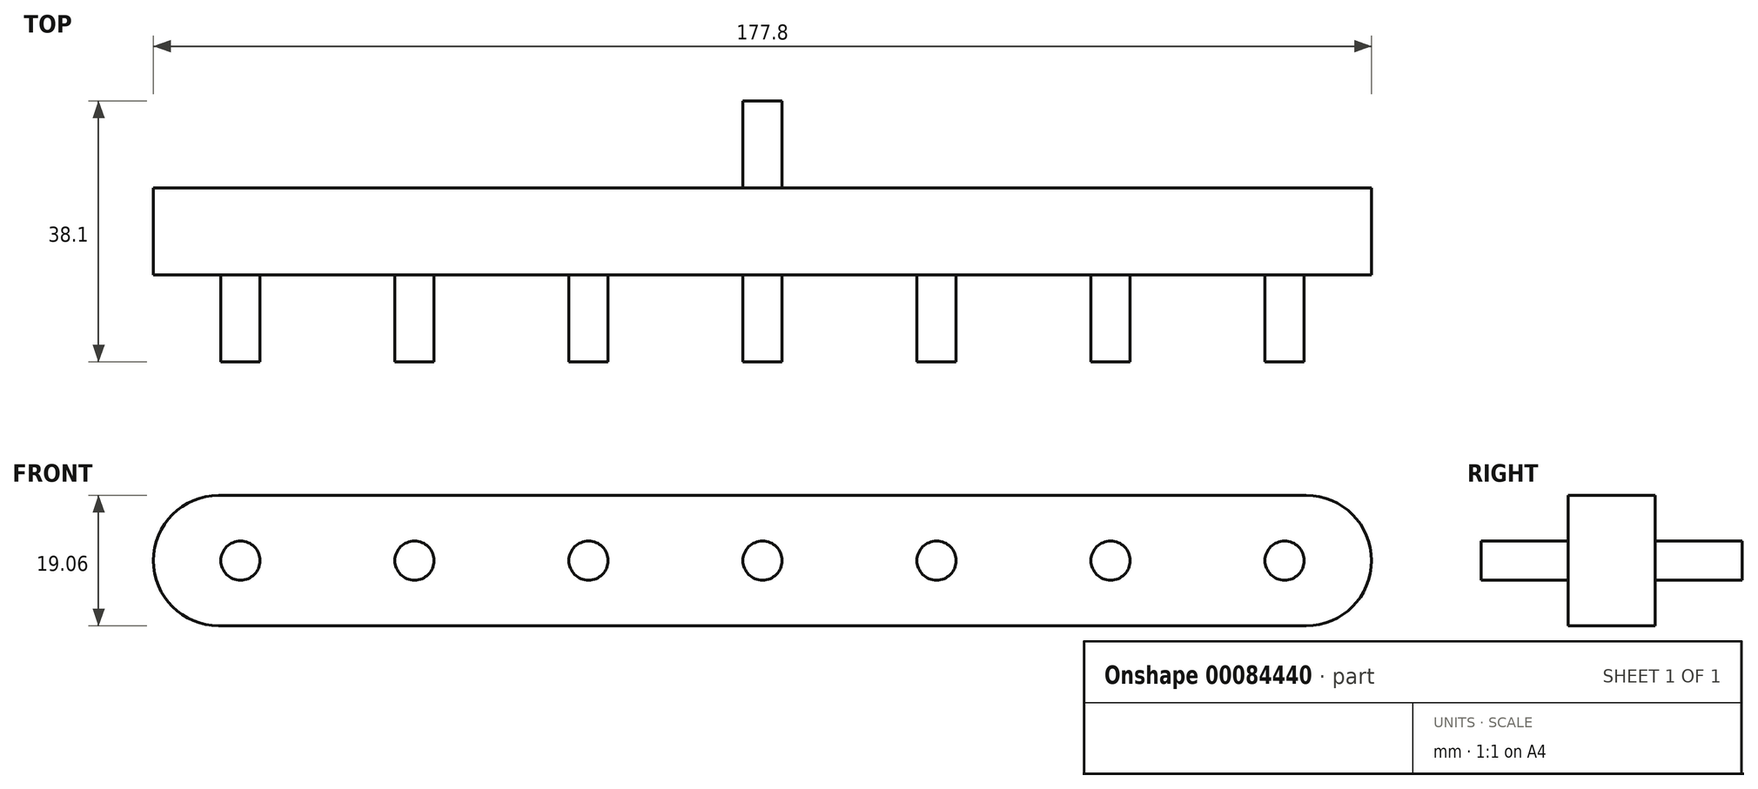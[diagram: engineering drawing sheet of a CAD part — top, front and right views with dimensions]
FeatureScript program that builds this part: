
annotation { "Feature Type Name" : "Feature", "Feature Type Description" : "" }
export const myFeature = defineFeature(function(context is Context, id is Id, definition is map)
    precondition{}
    {
        {
            var Q0;
            Q0=qCreatedBy(makeId("Front.planeOp"),FACE);
            var sketch = newSketch(context, id + "F0", { "sketchPlane" : qUnion([Q0])});
            skLineSegment(sketch, "E0.bottom", {"start": v(88.9, -9.52) * mm, "end": v(-88.9, -9.52) * mm});
            skLineSegment(sketch, "E0.top", {"start": v(88.9, 9.53) * mm, "end": v(-88.9, 9.53) * mm});
            skLineSegment(sketch, "E0.left", {"start": v(88.9, -9.52) * mm, "end": v(88.9, 9.53) * mm});
            skLineSegment(sketch, "E0.right", {"start": v(-88.9, -9.52) * mm, "end": v(-88.9, 9.53) * mm});
            skPoint(sketch, "E1.middle", {"position": v(0, 0) * mm});
            skLineSegment(sketch, "E2", {"start": v(0, 0) * mm, "end": v(0, 0) * mm});
            skCircle(sketch, "E3", {"center": v(0, 0) * mm, "radius": 2.86 * mm});
            skCircle(sketch, "E4.1.0.0", {"center": v(25.4, 0) * mm, "radius": 2.86 * mm});
            skCircle(sketch, "E4.2.0.0", {"center": v(50.8, 0) * mm, "radius": 2.86 * mm});
            skLineSegment(sketch, "E4.direction1", {"start": v(0, 0) * mm, "end": v(25.4, 0) * mm, "construction": true});
            skCircle(sketch, "E5.0.3.0", {"center": v(76.2, 0) * mm, "radius": 2.86 * mm});
            skCircle(sketch, "E6.1.0.0", {"center": v(-25.4, 0) * mm, "radius": 2.86 * mm});
            skCircle(sketch, "E6.2.0.0", {"center": v(-50.8, 0) * mm, "radius": 2.86 * mm});
            skLineSegment(sketch, "E6.direction1", {"start": v(0, 0) * mm, "end": v(-25.4, 0) * mm, "construction": true});
            skCircle(sketch, "E7.0.3.0", {"center": v(-76.2, 0) * mm, "radius": 2.86 * mm});
            skLineSegment(sketch, "E8", {"start": v(0, 0) * mm, "end": v(0, 9.53) * mm});
            skSolve(sketch);
        }
        {
            var Q0;
            Q0=makeQuery(id+"F0.imprint","IMPRINT",FACE,{"disambiguationData":[TD([[makeQuery(id+"F0.imprint","IMPRINT",EDGE,{"derivedFrom":sQuery(id+"F0.wireOp",EDGE,"SHm8Pa34-JDRi-xLCb-vY8M-4y8iot5nddfY")}),1.0]])]});
            var Q1;
            Q1=makeQuery(id+"F0.imprint","IMPRINT",FACE,{"disambiguationData":[TD([[makeQuery(id+"F0.imprint","IMPRINT",EDGE,{"derivedFrom":sQuery(id+"F0.wireOp",EDGE,"E0.bottom")}),-1.0]])]});
            var Q2;
            Q2=makeQuery(id+"F0.imprint","IMPRINT",FACE,{"disambiguationData":[TD([[makeQuery(id+"F0.imprint","IMPRINT",EDGE,{"derivedFrom":sQuery(id+"F0.wireOp",EDGE,"yVfw5L5J-6KiR-xsoj-KyT5-XFOPuA5cFtkD")}),1.0]])]});
            var Q3;
            Q3=makeQuery(id+"F0.imprint","IMPRINT",FACE,{"disambiguationData":[TD([[makeQuery(id+"F0.imprint","IMPRINT",EDGE,{"derivedFrom":sQuery(id+"F0.wireOp",EDGE,"otzoMOgJ-2Fw9-6XRC-HHPs-JyfjwHity7ub")}),1.0]])]});
            extrude(context, id + "F1", {"entities" : qUnion([Q0, Q1, Q2, Q3]), "depth" : 12.7 * mm});
        }
        {
            var Q0;
            Q0=makeQuery(id+"F0.imprint","IMPRINT",FACE,{"disambiguationData":[TD([[makeQuery(id+"F0.imprint","IMPRINT",EDGE,{"derivedFrom":sQuery(id+"F0.wireOp",EDGE,"E3")}),1.0]])]});
            var Q1;
            Q1=makeQuery(id+"F0.imprint","IMPRINT",FACE,{"disambiguationData":[TD([[makeQuery(id+"F0.imprint","IMPRINT",EDGE,{"derivedFrom":sQuery(id+"F0.wireOp",EDGE,"W0BhPmkZ-Cohu-r3UB-MNsT-8zEHgvukqrbW")}),1.0]])]});
            var Q2;
            Q2=makeQuery(id+"F0.imprint","IMPRINT",FACE,{"disambiguationData":[TD([[makeQuery(id+"F0.imprint","IMPRINT",EDGE,{"derivedFrom":sQuery(id+"F0.wireOp",EDGE,"otzoMOgJ-2Fw9-6XRC-HHPs-JyfjwHity7ub")}),1.0]])]});
            var Q3;
            Q3=makeQuery(id+"F0.imprint","IMPRINT",FACE,{"disambiguationData":[TD([[makeQuery(id+"F0.imprint","IMPRINT",EDGE,{"derivedFrom":sQuery(id+"F0.wireOp",EDGE,"3Px4a1Am-neuG-O9X5-1E42-bK21xOlIPYbs")}),1.0]])]});
            var Q4;
            Q4=makeQuery(id+"F0.imprint","IMPRINT",FACE,{"disambiguationData":[TD([[makeQuery(id+"F0.imprint","IMPRINT",EDGE,{"derivedFrom":sQuery(id+"F0.wireOp",EDGE,"TvybUxnP-oc0P-UiPS-1L8a-IxXoS0crJDyP")}),1.0]])]});
            var Q5;
            Q5=makeQuery(id+"F0.imprint","IMPRINT",FACE,{"disambiguationData":[TD([[makeQuery(id+"F0.imprint","IMPRINT",EDGE,{"derivedFrom":sQuery(id+"F0.wireOp",EDGE,"yVfw5L5J-6KiR-xsoj-KyT5-XFOPuA5cFtkD")}),1.0]])]});
            var Q6;
            Q6=makeQuery(id+"F0.imprint","IMPRINT",FACE,{"disambiguationData":[TD([[makeQuery(id+"F0.imprint","IMPRINT",EDGE,{"derivedFrom":sQuery(id+"F0.wireOp",EDGE,"E7.0.4.0")}),1.0]])]});
            var Q7;
            Q7=makeQuery(id+"F0.imprint","IMPRINT",FACE,{"disambiguationData":[TD([[makeQuery(id+"F0.imprint","IMPRINT",EDGE,{"derivedFrom":sQuery(id+"F0.wireOp",EDGE,"E7.0.3.0")}),1.0]])]});
            var Q8;
            Q8=makeQuery(id+"F0.imprint","IMPRINT",FACE,{"disambiguationData":[TD([[makeQuery(id+"F0.imprint","IMPRINT",EDGE,{"derivedFrom":sQuery(id+"F0.wireOp",EDGE,"E6.2.0.0")}),1.0]])]});
            var Q9;
            Q9=makeQuery(id+"F0.imprint","IMPRINT",FACE,{"disambiguationData":[TD([[makeQuery(id+"F0.imprint","IMPRINT",EDGE,{"derivedFrom":sQuery(id+"F0.wireOp",EDGE,"E6.1.0.0")}),1.0]])]});
            var Q10;
            Q10=makeQuery(id+"F0.imprint","IMPRINT",FACE,{"disambiguationData":[TD([[makeQuery(id+"F0.imprint","IMPRINT",EDGE,{"derivedFrom":sQuery(id+"F0.wireOp",EDGE,"E4.1.0.0")}),1.0]])]});
            var Q11;
            Q11=makeQuery(id+"F0.imprint","IMPRINT",FACE,{"disambiguationData":[TD([[makeQuery(id+"F0.imprint","IMPRINT",EDGE,{"derivedFrom":sQuery(id+"F0.wireOp",EDGE,"E4.2.0.0")}),1.0]])]});
            var Q12;
            Q12=makeQuery(id+"F0.imprint","IMPRINT",FACE,{"disambiguationData":[TD([[makeQuery(id+"F0.imprint","IMPRINT",EDGE,{"derivedFrom":sQuery(id+"F0.wireOp",EDGE,"E5.0.3.0")}),1.0]])]});
            var Q13;
            Q13=makeQuery(id+"F0.imprint","IMPRINT",FACE,{"disambiguationData":[TD([[makeQuery(id+"F0.imprint","IMPRINT",EDGE,{"derivedFrom":sQuery(id+"F0.wireOp",EDGE,"E5.0.4.0")}),1.0]])]});
            extrude(context, id + "F2", {"entities" : qUnion([Q0, Q1, Q2, Q3, Q4, Q5, Q6, Q7, Q8, Q9, Q10, Q11, Q12, Q13]), "operationType" : NewBodyOperationType.ADD, "depth" : 25.4 * mm});
        }
        {
            var Q0;
            {var subQ0=sQuery(id+"F0.wireOp",EDGE,"3Px4a1Am-neuG-O9X5-1E42-bK21xOlIPYbs");var subQ1=sQuery(id+"F0.wireOp",EDGE,"E3");var subQ2=sQuery(id+"F0.wireOp",EDGE,"TvybUxnP-oc0P-UiPS-1L8a-IxXoS0crJDyP");Q0=makeQuery(id+"F2.boolean.opBoolean","MERGE",FACE,{"derivedFrom":[makeQuery(id+"F1.opExtrude","CAP_FACE",FACE,{"disambiguationData":[OSD([sQuery(id+"F0.wireOp",EDGE,"E0.bottom"),sQuery(id+"F0.wireOp",EDGE,"E0.top"),sQuery(id+"F0.wireOp",EDGE,"E0.left"),sQuery(id+"F0.wireOp",EDGE,"E0.right"),subQ2,subQ1,subQ0])],"isStart":true}),makeQuery(id+"F2.opExtrude","CAP_FACE",FACE,{"disambiguationData":[OSD([subQ2])],"isStart":true}),makeQuery(id+"F2.opExtrude","CAP_FACE",FACE,{"disambiguationData":[OSD([subQ1])],"isStart":true}),makeQuery(id+"F2.opExtrude","CAP_FACE",FACE,{"disambiguationData":[OSD([subQ0])],"isStart":true})]});}
            var sketch = newSketch(context, id + "F3", { "sketchPlane" : qUnion([Q0])});
            skLineSegment(sketch, "E9", {"start": v(0, 0) * mm, "end": v(0, 0) * mm});
            skCircle(sketch, "E10", {"center": v(0, 0) * mm, "radius": 2.86 * mm});
            skSolve(sketch);
        }
        {
            var Q0;
            Q0=makeQuery(id+"F3.imprint","IMPRINT",FACE,{"disambiguationData":[TD([[makeQuery(id+"F3.imprint","IMPRINT",EDGE,{"derivedFrom":makeQuery(id+"F1.opExtrude","CAP_EDGE",EDGE,{"disambiguationData":[OSD([sQuery(id+"F0.wireOp",EDGE,"E7.0.3.0")])],"isStart":true})}),-1.0]])]});
            var Q1;
            Q1=makeQuery(id+"F3.imprint","IMPRINT",FACE,{"disambiguationData":[TD([[makeQuery(id+"F3.imprint","IMPRINT",EDGE,{"derivedFrom":sQuery(id+"F3.wireOp",EDGE,"E10")}),1.0]])]});
            extrude(context, id + "F4", {"entities" : qUnion([Q0, Q1]), "operationType" : NewBodyOperationType.ADD, "depth" : 12.7 * mm});
        }
        {
            var Q0;
            Q0=makeQuery(id+"F1.opExtrude","SWEPT_EDGE",EDGE,{"disambiguationData":[OSD([sQuery(id+"F0.wireOp",EDGE,"E0.top"),sQuery(id+"F0.wireOp",EDGE,"E0.left")])]});
            var Q1;
            Q1=makeQuery(id+"F1.opExtrude","SWEPT_EDGE",EDGE,{"disambiguationData":[OSD([sQuery(id+"F0.wireOp",EDGE,"E0.bottom"),sQuery(id+"F0.wireOp",EDGE,"E0.left")])]});
            var Q2;
            Q2=makeQuery(id+"F1.opExtrude","SWEPT_EDGE",EDGE,{"disambiguationData":[OSD([sQuery(id+"F0.wireOp",EDGE,"E0.bottom"),sQuery(id+"F0.wireOp",EDGE,"E0.right")])]});
            var Q3;
            Q3=makeQuery(id+"F1.opExtrude","SWEPT_EDGE",EDGE,{"disambiguationData":[OSD([sQuery(id+"F0.wireOp",EDGE,"E0.top"),sQuery(id+"F0.wireOp",EDGE,"E0.right")])]});
            fillet(context, id + "F5", {"entities" : qUnion([Q0, Q1, Q2, Q3]), "radius" : 9.52 * mm, "tangentPropagation" : true, "allowEdgeOverflow" : false});
        }
    });
